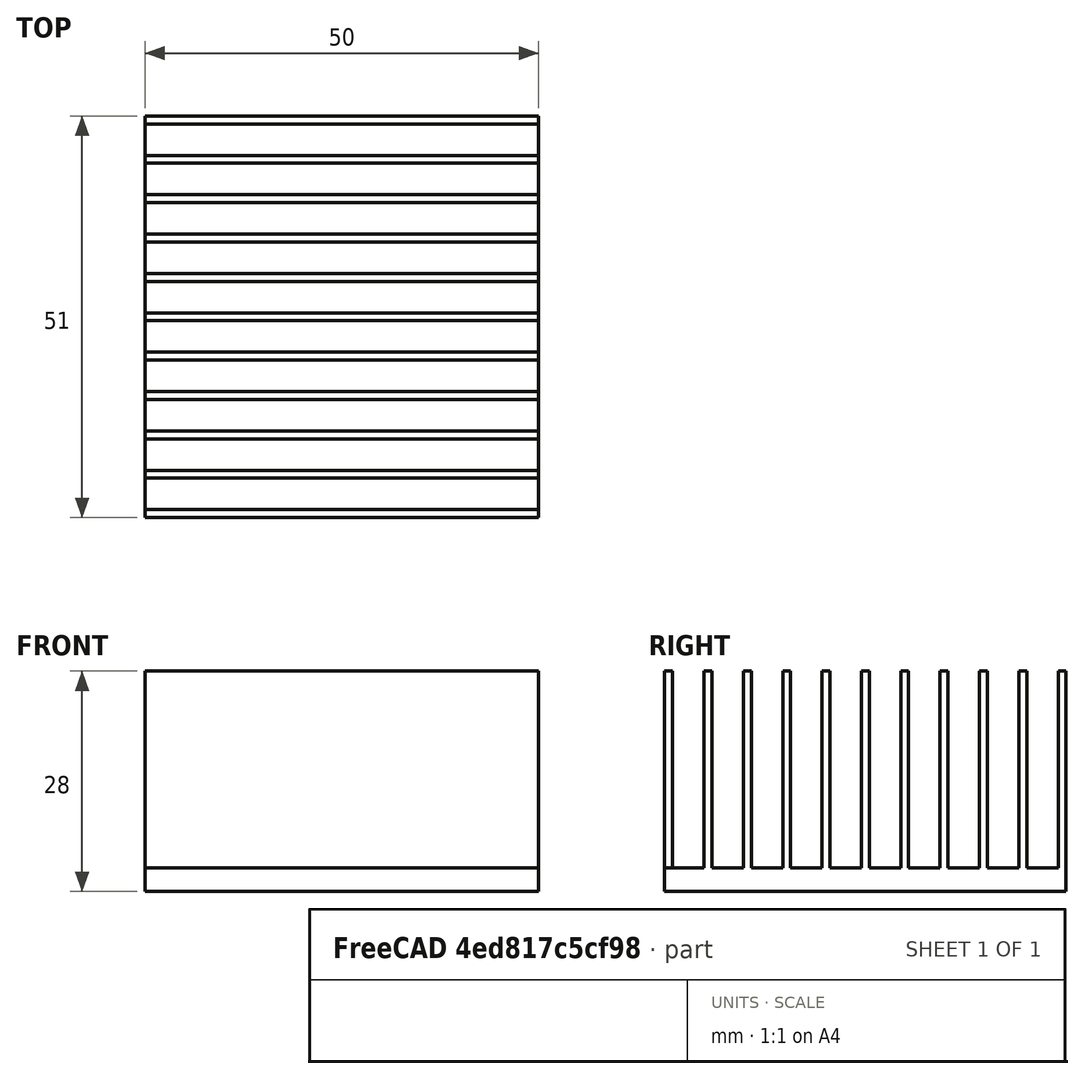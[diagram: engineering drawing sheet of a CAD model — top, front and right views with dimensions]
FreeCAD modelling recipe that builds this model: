
FCSTD DOCUMENT  (FreeCAD 0.20R26498 (Git))
Label: 230 - HEAT SINK
License: All rights reserved
LicenseURL: http://en.wikipedia.org/wiki/All_rights_reserved
objects: Part::Box×2, Part::Cylinder×1, Part::FeaturePython×1, Part::MultiFuse×1, Fem::FemSolverObjectPython×1, App::MaterialObjectPython×1, Fem::ConstraintInitialTemperature×1, Fem::ConstraintHeatflux×1, Fem::ConstraintTemperature×1, Fem::FemMeshShapeNetgenObject×1, Fem::FemMeshObjectPython×1, Fem::FemResultObjectPython×1, Fem::FemAnalysis×1
note: 4 computed .brp shape members not serialized (recipe doc carries the construction recipe); baked Part::Feature solids carry a one-line shape summary decoded from their .brp

FEATURE [Part::Box] Box  label="Cube"
  AttacherType = Attacher::AttachEngine3D
  Height = 3
  Length = 50
  Placement = pos=(-25,-25,0) rot=(0,0,1;0rad)
  Width = 51
FEATURE [Part::Cylinder] Cylinder
  Angle = 360
  AttacherType = Attacher::AttachEngine3D
  FirstAngle = 0
  Height = 2
  Radius = 10
  SecondAngle = 0
FEATURE [Part::Box] Box001  label="Cube001"
  AttacherType = Attacher::AttachEngine3D
  Height = 25
  Length = 50
  Placement = pos=(-25,-25,3) rot=(0,0,1;0rad)
  Width = 1
FEATURE [Part::FeaturePython] Array  # Draft array (typed FeaturePython)
  Angle = 360
  ArrayType = 0
  Axis = (0,0,1)
  Base = -> Box001
  Center = (0,0,0)
  Count = 11
  ExpandArray = false
  Fuse = false
  IntervalAxis = (0,0,0)
  IntervalX = (100,0,0)
  IntervalY = (0,5,0)
  IntervalZ = (0,0,100)
  NumberCircles = 3
  NumberPolar = 5
  NumberX = 1
  NumberY = 11
  NumberZ = 1
  PlacementList = 11 placements: arithmetic series from (-25,-25,3) step (0,5,0) to (-25,25,3)
  RadialDistance = 50
  ScaleList = (11) [(1,1,1),(1,1,1),(1,1,1),(1,1,1),(1,1,1),(1,1,1),(1,1,1),(1,1,1),(1,1,1),(1,1,1),(1,1,1)]
  Symmetry = 1
  TangentialDistance = 25
FEATURE [Part::MultiFuse] Fusion
  Shapes = -> [Array,Cylinder,Box]
FEATURE [Fem::FemSolverObjectPython] SolverCcxTools  # FEM object (typed FeaturePython)
  AnalysisType = 2
  BeamShellResultOutput3D = false
  BucklingFactors = 1
  EigenmodeHighLimit = 1000000
  EigenmodeLowLimit = 0
  EigenmodesCount = 10
  GeometricalNonlinearity = 0
  IterationsControlParameterCutb = 0.25,0.5,0.75,0.85,,,1.5,
  IterationsControlParameterIter = 4,8,9,200,10,400,,200,,
  IterationsControlParameterTimeUse = false
  IterationsThermoMechMaximum = 2000
  IterationsUserDefinedIncrementations = false
  IterationsUserDefinedTimeStepLength = false
  MaterialNonlinearity = 0
  MatrixSolverType = 0
  SplitInputWriter = false
  ThermoMechSteadyState = true
  TimeEnd = 1
  TimeInitialStep = 1
FEATURE [App::MaterialObjectPython] MaterialSolid  # material (typed FeaturePython)
  Category = 0
  Material = AuthorAndLicense=(c) 2016 Mandeep Singh (CC-BY 3.0),CardName=Aluminum-6061-T6,Density=2700 kg/m^3,+12 more (map truncated)
FEATURE [Fem::ConstraintInitialTemperature] ConstraintInitialTemperature
  NormalDirection = (0,0,1)
  initialTemperature = 300
FEATURE [Fem::ConstraintHeatflux] ConstraintHeatflux
  AmbientTemp = 300
  ConstraintType = 1
  DFlux = 0
  FilmCoef = 10
  NormalDirection = (0,-1,0)
  Normals = (868) [(0,-1,0),(0,-1,0),(0,-1,0),(0,-1,0),(0,-1,0),(0,-1,0),(0,-1,0),(0,-1,0),(0,-1,0),(0,-1,0),(0,-1,0),(0,-1,0),(0,-1,0),(0,-1,0),(0,-1,0),(0,-1,0),+852 more]
  Points = (868) [(-25,-25,3),(-25,-25,11.3333),(-25,-25,19.6667),(-25,-25,28),(-8.33333,-25,3),(-8.33333,-25,11.3333),(-8.33333,-25,19.6667),(-8.33333,-25,28),+860 more]
  References = -> [Fusion]
  Scale = 3
FEATURE [Fem::ConstraintTemperature] ConstraintTemperature
  CFlux = 5000000
  ConstraintType = 0
  NormalDirection = (0,0,-1)
  Normals = (5) [(0,0,-1),(0,0,-1),(0,0,-1),(0,0,-1),(0,0,-1)]
  Points = (5) [(0,-10,0),(-10,0,0),(0,0,0),(10,0,0),(0,10,0)]
  References = -> [Fusion]
  Temperature = 300
FEATURE [Fem::FemMeshShapeNetgenObject] FEMMeshNetgen
  Fineness = 2
  GrowthRate = 0.3
  MaxSize = 1000
  NbSegsPerEdge = 1
  NbSegsPerRadius = 2
  Optimize = true
  SecondOrder = true
  Shape = -> Fusion
FEATURE [Fem::FemMeshObjectPython] ResultMesh  # FEM object (typed FeaturePython)
FEATURE [Fem::FemResultObjectPython] CCX_Results  # FEM object (typed FeaturePython)
  DisplacementLengths = [0.0656351,0.0647891,0.0613567,0.0605159,0.0570824,0.056248,0.0528252,0.0519982,0.0486186,0.0478017,0.0445126,0.0437094,0.0405291,0.0397452,0.0366805,0.0359226,0.0329757,0.0322528,0.0294567,0.0287827,0.0262042,0.0255993,0.0491515,0.0782461,+94042 more]
  DisplacementVectors = (94066) [(-0.000984996,0.0288765,-0.0589334),(-0.000713172,0.0285101,-0.0581747),(0.000406347,0.0269893,-0.0551004),(0.000678132,0.0266214,-0.0543417),+94062 more]
  Eigenmode = 0
  EigenmodeFrequency = 0
  MaxShear = [0.000802506,0.000521609,0.000725705,0.00110615,0.000783955,0.00050496,0.000660887,0.00101265,0.000699492,0.000383205,0.000588981,0.000838176,0.000739086,0.000353069,0.000721224,0.000888874,0.000895671,0.000445779,0.000850816,0.000964791,+94046 more]
  Mesh = -> ResultMesh
  NodeNumbers = [1,2,3,4,5,6,7,8,9,10,11,12,13,14,15,16,17,18,19,20,21,22,23,24,25,26,27,28,29,30,31,32,33,34,35,36,37,38,39,40,41,42,43,44,45,46,47,48,49,50,51,52,53,54,55,56,57,58,59,60,61,62,63,64,65,66,67,68,69,+93997 more]
  NodeStrainXX = [0.000366408,0.000366407,0.000367854,0.000367844,0.000370503,0.000370503,0.000374411,0.000374402,0.000378407,0.000378407,0.000380249,0.00038024,0.000379257,0.000379256,0.00037594,0.000375928,0.000372132,0.00037213,0.000369493,0.000369481,+94046 more]
  NodeStrainXY = [-4.75309e-10,-1.51596e-09,-3.0913e-10,2.18127e-09,-5.43209e-10,-1.49874e-09,-6.42998e-10,1.60219e-09,-8.50573e-10,-1.31084e-09,-7.76241e-10,6.57076e-10,-8.53994e-10,-1.27247e-09,3.22448e-10,7.92222e-10,-5.10857e-10,-1.43739e-09,1.22111e-09,+94047 more]
  NodeStrainXZ = [-1.5106e-08,-8.63707e-09,-1.34876e-08,-1.99729e-08,-1.47383e-08,-8.34775e-09,-1.2268e-08,-1.84149e-08,-1.3112e-08,-6.27591e-09,-1.06869e-08,-1.5278e-08,-1.39612e-08,-5.78565e-09,-1.31941e-08,-1.58208e-08,-1.71188e-08,-7.40463e-09,+94048 more]
  NodeStrainYY = [0.000366395,0.000366398,0.000367838,0.000367837,0.000370491,0.000370494,0.000374397,0.000374397,0.000378398,0.0003784,0.000380237,0.000380239,0.000379247,0.00037925,0.000375924,0.000375925,0.000372118,0.000372122,0.000369475,0.000369474,+94046 more]
  NodeStrainYZ = [5.72541e-11,-1.76429e-09,1.11391e-09,-3.06927e-09,-1.55414e-10,-1.70732e-09,6.57399e-10,-2.09791e-09,-7.36956e-10,-1.24435e-09,1.61506e-10,-6.04317e-10,-5.02206e-10,-1.05551e-09,7.10831e-10,-9.16151e-10,5.03822e-10,-1.28505e-09,1.28608e-09,+94047 more]
  NodeStrainZZ = [0.000366413,0.000366408,0.000367847,0.000367858,0.000370508,0.000370503,0.000374405,0.000374414,0.000378411,0.000378407,0.000380242,0.00038025,0.000379261,0.000379257,0.000375932,0.000375941,0.000372137,0.000372131,0.000369485,0.000369496,+94046 more]
  NodeStressXX = [0.000563319,0.000336251,0.000761845,0.000375897,0.000532919,0.000323018,0.000695667,0.000269478,0.000415102,0.000232052,0.000620321,0.00010463,0.00045912,0.000210168,0.000756503,0.00015509,0.00066001,0.000280191,0.000875275,0.000251249,+94046 more]
  NodeStressXY = [-2.46589e-05,-7.86474e-05,-1.60376e-05,0.000113164,-2.81815e-05,-7.77544e-05,-3.33586e-05,8.31211e-05,-4.41275e-05,-6.80058e-05,-4.02712e-05,3.40889e-05,-4.4305e-05,-6.60154e-05,1.67285e-05,4.11002e-05,-2.65031e-05,-7.45714e-05,6.33506e-05,+94047 more]
  NodeStressXZ = [-0.000783694,-0.000448088,-0.000699731,-0.00103619,-0.00076462,-0.000433079,-0.000636458,-0.000955358,-0.000680249,-0.000325592,-0.000554433,-0.000792618,-0.000724305,-0.000300158,-0.000684506,-0.00082078,-0.000888119,-0.00038415,+94048 more]
  NodeStressYY = [-8.20113e-05,-0.000146381,-3.34555e-05,-3.37451e-05,-7.4179e-05,-0.000143111,-2.22642e-05,1.51747e-05,-4.72773e-05,-0.00011433,-1.38397e-05,6.39768e-05,-5.69889e-05,-0.000104348,-4.13549e-05,-1.73066e-05,-0.000103493,-0.000121909,+94048 more]
  NodeStressYZ = [2.97032e-06,-9.15308e-05,5.77892e-05,-0.000159233,-8.06283e-06,-8.85754e-05,3.41057e-05,-0.000108839,-3.82331e-05,-6.45563e-05,8.37886e-06,-3.13518e-05,-2.60543e-05,-5.47598e-05,3.68777e-05,-4.75296e-05,2.61381e-05,-6.66678e-05,6.67214e-05,+94047 more]
  NodeStressZZ = [0.000843576,0.000363182,0.000436174,0.00109021,0.000803907,0.000350884,0.000348101,0.000904527,0.000619298,0.000266223,0.00023245,0.000643718,0.000641293,0.00025109,0.000339982,0.000829805,0.000883331,0.000325422,0.000457939,0.00104279,+94046 more]
  PrincipalMax = [0.00149978,0.000798135,0.00131918,0.00184933,0.00144504,0.000770356,0.00118349,0.00160553,0.00120507,0.000575177,0.00101514,0.00121316,0.00128029,0.000531524,0.00126378,0.00138263,0.00166756,0.00068763,0.00148926,0.00161516,0.00177178,+94045 more]
  PrincipalMed = [-6.96601e-05,3.45933e-10,-2.23804e-05,-5.40101e-05,-5.95209e-05,-5.32433e-10,-2.37009e-05,3.42314e-06,-2.40298e-05,2.32382e-10,-1.33845e-05,6.23582e-05,-3.89797e-05,-4.91687e-10,-2.99918e-05,-1.99277e-05,-0.00010393,1.83945e-10,+94048 more]
  PrincipalMin = [-0.000105234,-0.000245083,-0.000132233,-0.000362963,-0.000122871,-0.000239564,-0.000138285,-0.000419773,-0.000193916,-0.000191233,-0.000162824,-0.000463192,-0.000197884,-0.000174614,-0.000178663,-0.000395116,-0.000123782,-0.000203927,+94048 more]
  ResultType = Fem::ResultMechanical
  Stats = [-0.0604997,0.0128585,-0.0255756,0.0288765,-0.0692753,0.0529677,0.00141601,0.0811082,9.39894e-05,0.90451,-0.0761491,0.856991,-0.652271,0.111552,-0.699393,0.0765793,5.32732e-05,0.474145,0,0,315.862,317.509,0,0,0,0]
  Temperature = [315.862,315.862,315.924,315.924,316.039,316.039,316.208,316.208,316.381,316.381,316.461,316.461,316.418,316.418,316.274,316.274,316.11,316.11,315.995,315.995,315.933,315.933,317.149,316.277,316.308,315.864,315.864,316.329,316.286,315.927,+94036 more]
  Time = 1
  vonMises = [0.00158752,0.000944825,0.00139972,0.00207514,0.00153721,0.000913996,0.00126837,0.00185036,0.00132225,0.000690935,0.00111081,0.00148504,0.00140547,0.00063704,0.00137416,0.00162301,0.0017815,0.000809103,0.00160898,0.00183341,0.00188038,+94045 more]
FEATURE [Fem::FemAnalysis] Analysis
  Group = -> [SolverCcxTools,MaterialSolid,ConstraintInitialTemperature,ConstraintHeatflux,ConstraintTemperature,FEMMeshNetgen,CCX_Results]
